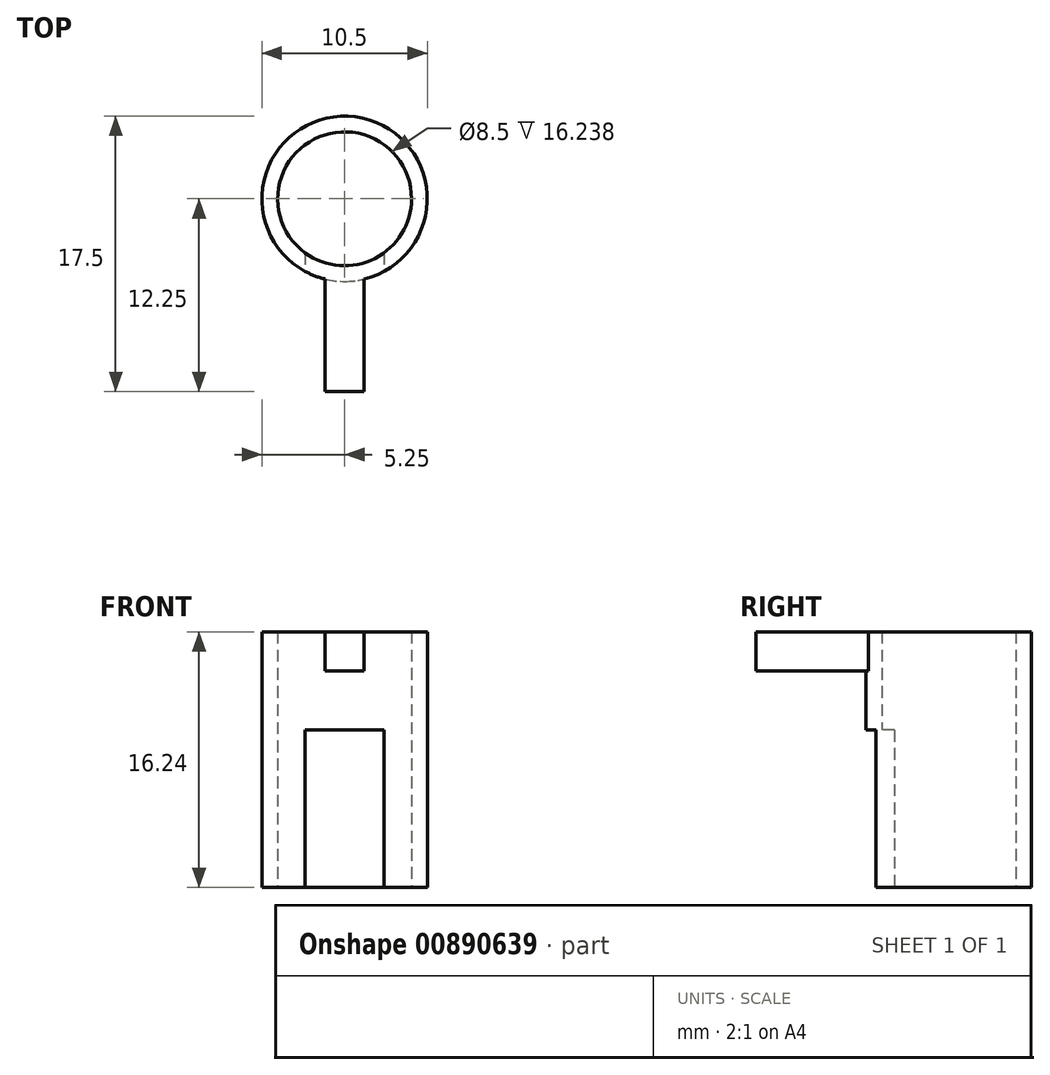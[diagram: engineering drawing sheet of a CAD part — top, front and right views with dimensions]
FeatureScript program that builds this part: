
annotation { "Feature Type Name" : "Feature", "Feature Type Description" : "" }
export const myFeature = defineFeature(function(context is Context, id is Id, definition is map)
    precondition{}
    {
        {
            var Q0;
            Q0=qCreatedBy(makeId("Front.planeOp"),FACE);
            var sketch = newSketch(context, id + "F0", { "sketchPlane" : qUnion([Q0])});
            skCircle(sketch, "E0", {"center": v(0, 0) * mm, "radius": 1.75 * mm});
            skLineSegment(sketch, "E1.bottom", {"start": v(-1.24, 1.24) * mm, "end": v(1.24, 1.24) * mm});
            skLineSegment(sketch, "E1.top", {"start": v(-1.24, -1.24) * mm, "end": v(1.24, -1.24) * mm});
            skLineSegment(sketch, "E1.left", {"start": v(-1.24, 1.24) * mm, "end": v(-1.24, -1.24) * mm});
            skLineSegment(sketch, "E1.right", {"start": v(1.24, 1.24) * mm, "end": v(1.24, -1.24) * mm});
            skSolve(sketch);
        }
        {
            var Q0;
            Q0=qCreatedBy(makeId("Top.planeOp"),FACE);
            var sketch = newSketch(context, id + "F1", { "sketchPlane" : qUnion([Q0])});
            skCircle(sketch, "E2", {"center": v(0, 7.25) * mm, "radius": 4.25 * mm});
            skCircle(sketch, "E3", {"center": v(0, 7.25) * mm, "radius": 5.25 * mm});
            skSolve(sketch);
        }
        {
            var Q0;
            Q0=makeQuery(id+"F0.imprint","IMPRINT",FACE,{"disambiguationData":[TD([[makeQuery(id+"F0.imprint","IMPRINT",EDGE,{"derivedFrom":sQuery(id+"F0.wireOp",EDGE,"466c9b90-c97e-48b8-9ed6-756306f27bf7.0")}),-1.0]])]});
            var Q1;
            Q1=makeQuery(id+"F0.imprint","IMPRINT",FACE,{"disambiguationData":[TD([[makeQuery(id+"F0.imprint","IMPRINT",EDGE,{"derivedFrom":sQuery(id+"F0.wireOp",EDGE,"E1.bottom")}),-1.0]])]});
            extrude(context, id + "F2", {"entities" : qUnion([Q0, Q1]), "depth" : 5 * mm, "offsetDistance" : 25 * mm, "hasSecondDirection" : true, "secondDirectionOppositeDirection" : true, "secondDirectionDepth" : 2.25 * mm});
        }
        {
            var Q0;
            Q0=makeQuery(id+"F1.imprint","IMPRINT",FACE,{"disambiguationData":[TD([[makeQuery(id+"F1.imprint","IMPRINT",EDGE,{"derivedFrom":sQuery(id+"F1.wireOp",EDGE,"E2")}),-1.0]])]});
            var Q1;
            {var subQ0=sQuery(id+"F1.wireOp",EDGE,"84e436ee-733d-445b-aa2d-09ed9b8d7bc70.MirrorCS");Q1=makeQuery(id+"F1.imprint","IMPRINT",FACE,{"disambiguationData":[TD([[makeQuery(id+"F1.imprint","IMPRINT",EDGE,{"derivedFrom":subQ0}),-1.0]])]});}
            var Q2;
            {var subQ0=sQuery(id+"F1.wireOp",EDGE,"2Dlml9HW-Anqy-HuLk-2V8Z-CkaDEtIRr1xr");Q2=makeQuery(id+"F1.imprint","IMPRINT",FACE,{"disambiguationData":[TD([[makeQuery(id+"F1.imprint","IMPRINT",EDGE,{"derivedFrom":subQ0}),1.0]])]});}
            extrude(context, id + "F3", {"entities" : qUnion([Q0, Q1, Q2]), "operationType" : NewBodyOperationType.ADD, "depth" : 1.24 * mm, "offsetDistance" : 25 * mm, "hasSecondDirection" : true, "secondDirectionOppositeDirection" : true, "secondDirectionDepth" : 15 * mm});
        }
        {
            var Q0;
            Q0=qCreatedBy(makeId("Front.planeOp"),FACE);
            var sketch = newSketch(context, id + "F4", { "sketchPlane" : qUnion([Q0])});
            skLineSegment(sketch, "E4", {"start": v(0, -15) * mm, "end": v(0, -5) * mm});
            skLineSegment(sketch, "E5", {"start": v(-2.5, -5) * mm, "end": v(2.5, -5) * mm});
            skLineSegment(sketch, "E6", {"start": v(-2.5, -5) * mm, "end": v(-2.5, -15) * mm});
            skLineSegment(sketch, "E7", {"start": v(2.5, -5) * mm, "end": v(2.5, -15) * mm});
            skLineSegment(sketch, "E8", {"start": v(-2.5, -15) * mm, "end": v(2.5, -15) * mm});
            skSolve(sketch);
        }
        {
            var Q0;
            {var subQ0=sQuery(id+"F4.wireOp",EDGE,"E4");Q0=makeQuery(id+"F4.imprint","IMPRINT",FACE,{"disambiguationData":[TD([[makeQuery(id+"F4.imprint","IMPRINT",EDGE,{"derivedFrom":subQ0}),1.0]])]});}
            var Q1;
            {var subQ0=sQuery(id+"F4.wireOp",EDGE,"E4");Q1=makeQuery(id+"F4.imprint","IMPRINT",FACE,{"disambiguationData":[TD([[makeQuery(id+"F4.imprint","IMPRINT",EDGE,{"derivedFrom":subQ0}),-1.0]])]});}
            extrude(context, id + "F5", {"entities" : qUnion([Q0, Q1]), "operationType" : NewBodyOperationType.REMOVE, "oppositeDirection" : true, "depth" : 5 * mm, "offsetDistance" : 25 * mm});
        }
    });
